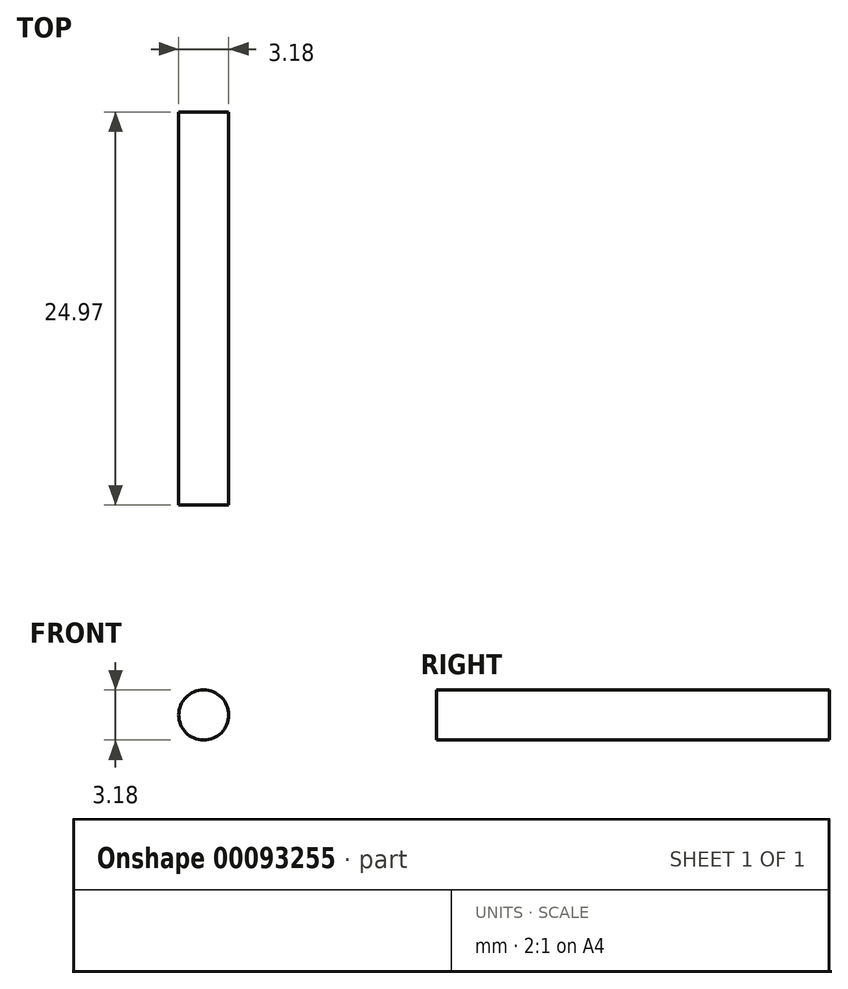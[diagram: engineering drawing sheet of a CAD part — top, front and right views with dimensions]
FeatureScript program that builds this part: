
annotation { "Feature Type Name" : "Feature", "Feature Type Description" : "" }
export const myFeature = defineFeature(function(context is Context, id is Id, definition is map)
    precondition{}
    {
        {
            var Q0;
            Q0=qCreatedBy(makeId("Front.planeOp"),FACE);
            var sketch = newSketch(context, id + "F0", { "sketchPlane" : qUnion([Q0])});
            skCircle(sketch, "E0", {"center": v(0, 0) * mm, "radius": 1.59 * mm});
            skSolve(sketch);
        }
        {
            var Q0;
            Q0 = qSketchRegion(id + "F0", true);
            extrude(context, id + "F1", {"entities" : qUnion([Q0]), "depth" : 24.97 * mm});
        }
    });
